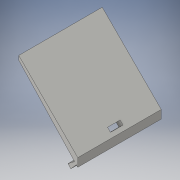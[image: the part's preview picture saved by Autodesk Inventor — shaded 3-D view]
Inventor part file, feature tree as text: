
AUTODESK INVENTOR PART (.ipt)
format: ipt  version: 2016 (Build 200138000, 138)  size: 120,320 bytes
history: native  units: in
note: dims shown in document units (in); Inventor stores cm internally (conversion verified against a paired STEP export)
features: extrude x3, sketch x2
ambient origin geometry x8: Origin, YZ Plane, XZ Plane, XY Plane, X Axis, Y Axis, Z Axis, Center Point
bodies: Solid1 (feature_tree)
feature tree (5):
  extrude  "Extrusion1"  TaperAngle=45.0deg  [1 undecoded]
  extrude  "Extrusion4"  Depth=0.5in
  extrude  "Extrusion5"  TaperAngle=90.0deg  [1 undecoded]
  sketch  "Sketch4"  dims[d0=5.0in d1=45.0deg]
  sketch  "Sketch5"  dims[d2=0.25in d5=0.5in d6=90.0deg d10=0.4in d12=5.0in d13=0.0in d24=0.75in d25=0.25in d26=1.0in d27=0.0in d28=0.4in d29=0.5in d30=0.15in d31=0.25in d32=4.5in d33=0.0in d34=0.2in]
note: 2 required parameter values undecoded (feature->parameter linkage not recoverable at this tier; creation-order binding heuristic only, values carry confidence <= 0.55)
